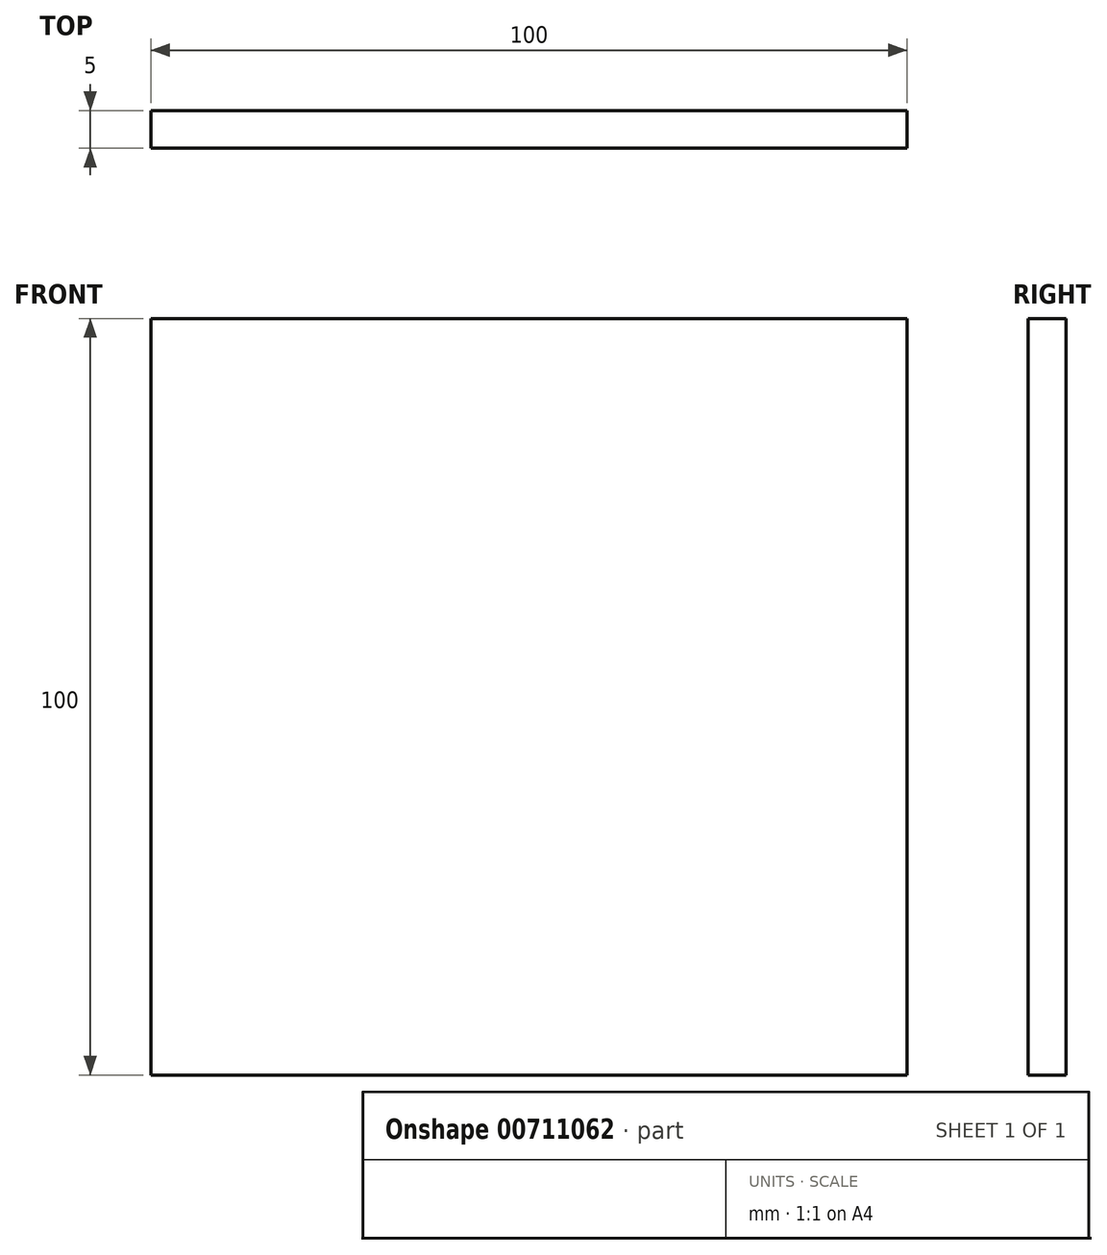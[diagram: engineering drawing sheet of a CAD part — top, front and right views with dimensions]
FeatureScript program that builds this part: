
annotation { "Feature Type Name" : "Feature", "Feature Type Description" : "" }
export const myFeature = defineFeature(function(context is Context, id is Id, definition is map)
    precondition{}
    {
        {
            var Q0;
            Q0=qCreatedBy(makeId("Front.planeOp"),FACE);
            var sketch = newSketch(context, id + "F0", { "sketchPlane" : qUnion([Q0])});
            skLineSegment(sketch, "E0", {"start": v(0, 0) * mm, "end": v(-275, 0) * mm});
            skLineSegment(sketch, "E1", {"start": v(-275, 0) * mm, "end": v(275, 0) * mm});
            skLineSegment(sketch, "E2.top", {"start": v(-275, 100) * mm, "end": v(275, 100) * mm});
            skLineSegment(sketch, "E2.left", {"start": v(-275, 0) * mm, "end": v(-275, 100) * mm});
            skLineSegment(sketch, "E2.right", {"start": v(275, 0) * mm, "end": v(275, 100) * mm});
            skLineSegment(sketch, "E3", {"start": v(-275, 100) * mm, "end": v(175, 100) * mm});
            skLineSegment(sketch, "E4", {"start": v(175, 100) * mm, "end": v(175, 0) * mm});
            skSolve(sketch);
        }
        {
            var Q0;
            Q0=makeQuery(id+"F0.imprint","IMPRINT",FACE,{"disambiguationData":[TD([[makeQuery(id+"F0.imprint","IMPRINT",EDGE,{"derivedFrom":sQuery(id+"F0.wireOp",EDGE,"E2.top")}),-1.0]])]});
            extrude(context, id + "F1", {"entities" : qUnion([Q0]), "depth" : 5 * mm, "offsetDistance" : 25.4 * mm});
        }
    });
